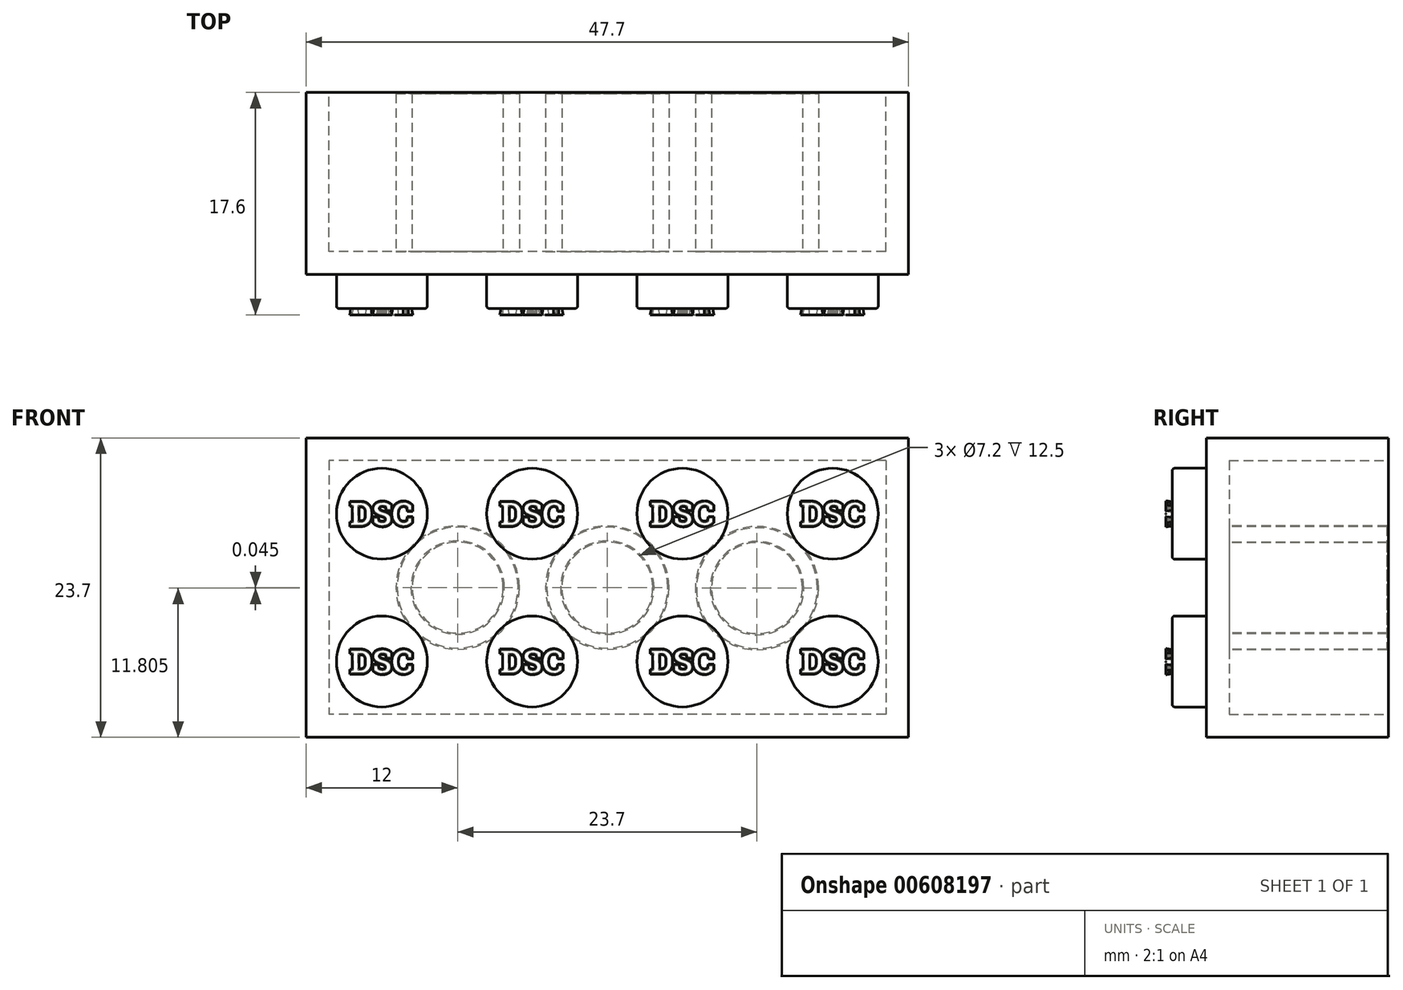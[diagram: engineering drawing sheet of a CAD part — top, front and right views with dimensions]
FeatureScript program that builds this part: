
annotation { "Feature Type Name" : "Feature", "Feature Type Description" : "" }
export const myFeature = defineFeature(function(context is Context, id is Id, definition is map)
    precondition{}
    {
        {
            var Q0;
            Q0=qCreatedBy(makeId("Front.planeOp"),FACE);
            var sketch = newSketch(context, id + "F0", { "sketchPlane" : qUnion([Q0])});
            skLineSegment(sketch, "E0.bottom", {"start": v(-23.85, 11.85) * mm, "end": v(23.85, 11.85) * mm});
            skLineSegment(sketch, "E0.top", {"start": v(-23.85, -11.85) * mm, "end": v(23.85, -11.85) * mm});
            skLineSegment(sketch, "E0.left", {"start": v(-23.85, 11.85) * mm, "end": v(-23.85, -11.85) * mm});
            skLineSegment(sketch, "E0.right", {"start": v(23.85, 11.85) * mm, "end": v(23.85, -11.85) * mm});
            skSolve(sketch);
        }
        {
            var Q0;
            Q0=makeQuery(id+"F0.imprint","IMPRINT",FACE,{"disambiguationData":[TD([[makeQuery(id+"F0.imprint","IMPRINT",EDGE,{"derivedFrom":sQuery(id+"F0.wireOp",EDGE,"E0.bottom")}),-1.0]])]});
            extrude(context, id + "F1", {"entities" : qUnion([Q0]), "depth" : 14.4 * mm, "offsetDistance" : 25 * mm});
        }
        {
            var Q0;
            Q0=makeQuery(id+"F1.opExtrude","CAP_FACE",FACE,{"disambiguationData":[OSD([sQuery(id+"F0.wireOp",EDGE,"E0.bottom"),sQuery(id+"F0.wireOp",EDGE,"E0.top"),sQuery(id+"F0.wireOp",EDGE,"E0.left"),sQuery(id+"F0.wireOp",EDGE,"E0.right")])],"isStart":true});
            var sketch = newSketch(context, id + "F2", { "sketchPlane" : qUnion([Q0])});
            skLineSegment(sketch, "E1.bottom", {"start": v(-22.05, 10.05) * mm, "end": v(22.05, 10.05) * mm});
            skLineSegment(sketch, "E1.top", {"start": v(-22.05, -10.05) * mm, "end": v(22.05, -10.05) * mm});
            skLineSegment(sketch, "E1.left", {"start": v(-22.05, 10.05) * mm, "end": v(-22.05, -10.05) * mm});
            skLineSegment(sketch, "E1.right", {"start": v(22.05, 10.05) * mm, "end": v(22.05, -10.05) * mm});
            skSolve(sketch);
        }
        {
            var Q0;
            Q0=makeQuery(id+"F2.imprint","IMPRINT",FACE,{"disambiguationData":[TD([[makeQuery(id+"F2.imprint","IMPRINT",EDGE,{"derivedFrom":sQuery(id+"F2.wireOp",EDGE,"E1.bottom")}),-1.0]])]});
            extrude(context, id + "F3", {"entities" : qUnion([Q0]), "operationType" : NewBodyOperationType.REMOVE, "oppositeDirection" : true, "depth" : 12.6 * mm, "offsetDistance" : 25 * mm});
        }
        {
            var Q0;
            Q0=makeQuery(id+"F1.opExtrude","CAP_FACE",FACE,{"disambiguationData":[OSD([sQuery(id+"F0.wireOp",EDGE,"E0.bottom"),sQuery(id+"F0.wireOp",EDGE,"E0.top"),sQuery(id+"F0.wireOp",EDGE,"E0.left"),sQuery(id+"F0.wireOp",EDGE,"E0.right")])],"isStart":false});
            var sketch = newSketch(context, id + "F4", { "sketchPlane" : qUnion([Q0])});
            skCircle(sketch, "E2", {"center": v(-17.85, 5.85) * mm, "radius": 3.6 * mm});
            skCircle(sketch, "E3.1.0.0", {"center": v(-5.95, 5.85) * mm, "radius": 3.6 * mm});
            skCircle(sketch, "E3.2.0.0", {"center": v(5.95, 5.85) * mm, "radius": 3.6 * mm});
            skCircle(sketch, "E3.3.0.0", {"center": v(17.85, 5.85) * mm, "radius": 3.6 * mm});
            skLineSegment(sketch, "E3.direction1", {"start": v(-17.85, 5.85) * mm, "end": v(-5.95, 5.85) * mm, "construction": true});
            skCircle(sketch, "E4", {"center": v(-17.85, -5.85) * mm, "radius": 3.6 * mm});
            skCircle(sketch, "E5.1.0.0", {"center": v(-5.95, -5.85) * mm, "radius": 3.6 * mm});
            skCircle(sketch, "E5.2.0.0", {"center": v(5.95, -5.85) * mm, "radius": 3.6 * mm});
            skLineSegment(sketch, "E5.direction1", {"start": v(-17.85, -5.85) * mm, "end": v(-5.95, -5.85) * mm, "construction": true});
            skCircle(sketch, "E6.0.3.0", {"center": v(17.85, -5.85) * mm, "radius": 3.6 * mm});
            skSolve(sketch);
        }
        {
            var Q0;
            Q0=makeQuery(id+"F4.imprint","IMPRINT",FACE,{"disambiguationData":[TD([[makeQuery(id+"F4.imprint","IMPRINT",EDGE,{"derivedFrom":sQuery(id+"F4.wireOp",EDGE,"E2")}),1.0]])]});
            var Q1;
            Q1=makeQuery(id+"F4.imprint","IMPRINT",FACE,{"disambiguationData":[TD([[makeQuery(id+"F4.imprint","IMPRINT",EDGE,{"derivedFrom":sQuery(id+"F4.wireOp",EDGE,"E3.1.0.0")}),1.0]])]});
            var Q2;
            Q2=makeQuery(id+"F4.imprint","IMPRINT",FACE,{"disambiguationData":[TD([[makeQuery(id+"F4.imprint","IMPRINT",EDGE,{"derivedFrom":sQuery(id+"F4.wireOp",EDGE,"E3.2.0.0")}),1.0]])]});
            var Q3;
            Q3=makeQuery(id+"F4.imprint","IMPRINT",FACE,{"disambiguationData":[TD([[makeQuery(id+"F4.imprint","IMPRINT",EDGE,{"derivedFrom":sQuery(id+"F4.wireOp",EDGE,"E3.3.0.0")}),1.0]])]});
            var Q4;
            Q4=makeQuery(id+"F4.imprint","IMPRINT",FACE,{"disambiguationData":[TD([[makeQuery(id+"F4.imprint","IMPRINT",EDGE,{"derivedFrom":sQuery(id+"F4.wireOp",EDGE,"E4")}),1.0]])]});
            var Q5;
            Q5=makeQuery(id+"F4.imprint","IMPRINT",FACE,{"disambiguationData":[TD([[makeQuery(id+"F4.imprint","IMPRINT",EDGE,{"derivedFrom":sQuery(id+"F4.wireOp",EDGE,"E5.1.0.0")}),1.0]])]});
            var Q6;
            Q6=makeQuery(id+"F4.imprint","IMPRINT",FACE,{"disambiguationData":[TD([[makeQuery(id+"F4.imprint","IMPRINT",EDGE,{"derivedFrom":sQuery(id+"F4.wireOp",EDGE,"E5.2.0.0")}),1.0]])]});
            var Q7;
            Q7=makeQuery(id+"F4.imprint","IMPRINT",FACE,{"disambiguationData":[TD([[makeQuery(id+"F4.imprint","IMPRINT",EDGE,{"derivedFrom":sQuery(id+"F4.wireOp",EDGE,"E6.0.3.0")}),1.0]])]});
            extrude(context, id + "F5", {"entities" : qUnion([Q0, Q1, Q2, Q3, Q4, Q5, Q6, Q7]), "depth" : 2.7 * mm, "offsetDistance" : 25 * mm});
        }
        {
            var Q0;
            Q0=makeQuery(id+"F5.opExtrude","CAP_FACE",FACE,{"disambiguationData":[OSD([sQuery(id+"F4.wireOp",EDGE,"E2")])],"isStart":false});
            var sketch = newSketch(context, id + "F6", { "sketchPlane" : qUnion([Q0])});
            skText(sketch, "E7", { "text": "DSC", "fontName": "RobotoSlab-Bold.ttf"});
            skPoint(sketch, "E8", {"position": v(-17.85, 5.85) * mm});
            skText(sketch, "E9", { "text": "DSC", "fontName": "RobotoSlab-Bold.ttf"});
            skPoint(sketch, "E10", {"position": v(-17.85, -5.85) * mm});
            skText(sketch, "E11", { "text": "DSC", "fontName": "RobotoSlab-Bold.ttf"});
            skPoint(sketch, "E12", {"position": v(-5.95, -5.85) * mm});
            skText(sketch, "E13", { "text": "DSC", "fontName": "RobotoSlab-Bold.ttf"});
            skPoint(sketch, "E14", {"position": v(-5.95, 5.85) * mm});
            skText(sketch, "E15", { "text": "DSC", "fontName": "RobotoSlab-Bold.ttf"});
            skPoint(sketch, "E16", {"position": v(5.95, 5.85) * mm});
            skPoint(sketch, "E17", {"position": v(5.95, -5.85) * mm});
            skPoint(sketch, "E18", {"position": v(17.85, 5.82) * mm});
            skText(sketch, "E19", { "text": "DSC", "fontName": "RobotoSlab-Bold.ttf"});
            skPoint(sketch, "E20", {"position": v(17.85, -5.85) * mm});
            skText(sketch, "E21", { "text": "DSC", "fontName": "RobotoSlab-Bold.ttf"});
            skPoint(sketch, "E22", {"position": v(17.85, 5.85) * mm});
            skText(sketch, "E23", { "text": "DSC", "fontName": "RobotoSlab-Bold.ttf"});
            const initialGuessF6  = {"E7": [-0.02038, 0.00492, 1, 0, 0.00185], "E9": [-0.02038, -0.00678, 1, 0, 0.00185], "E11": [-0.00848, -0.00678, 1, 0, 0.00185], "E13": [-0.00848, 0.00492, 1, 0, 0.00185], "E15": [0.00342, 0.00492, 1, 0, 0.00186], "E19": [0.01532, -0.00678, 1, 0, 0.00186], "E21": [0.01532, 0.00492, 1, 0, 0.00186], "E23": [0.00342, -0.00678, 1, 0, 0.00186]};
            skSetInitialGuess(sketch, initialGuessF6);
            skSolve(sketch);
        }
        {
            var Q0;
            Q0 = qSketchRegion(id + "F6", true);
            extrude(context, id + "F7", {"entities" : qUnion([Q0]), "depth" : 0.5 * mm, "offsetDistance" : 25 * mm, "hasDraft" : true, "draftAngle" : 10 * degree});
        }
        {
            var Q0;
            Q0=makeQuery(id+"F5.opExtrude","CAP_EDGE",EDGE,{"disambiguationData":[OSD([sQuery(id+"F4.wireOp",EDGE,"E2")])],"isStart":false});
            var Q1;
            Q1=makeQuery(id+"F5.opExtrude","CAP_EDGE",EDGE,{"disambiguationData":[OSD([sQuery(id+"F4.wireOp",EDGE,"E3.1.0.0")])],"isStart":false});
            var Q2;
            Q2=makeQuery(id+"F5.opExtrude","CAP_EDGE",EDGE,{"disambiguationData":[OSD([sQuery(id+"F4.wireOp",EDGE,"E3.2.0.0")])],"isStart":false});
            var Q3;
            Q3=makeQuery(id+"F5.opExtrude","CAP_EDGE",EDGE,{"disambiguationData":[OSD([sQuery(id+"F4.wireOp",EDGE,"E3.3.0.0")])],"isStart":false});
            var Q4;
            Q4=makeQuery(id+"F5.opExtrude","CAP_EDGE",EDGE,{"disambiguationData":[OSD([sQuery(id+"F4.wireOp",EDGE,"E6.0.3.0")])],"isStart":false});
            var Q5;
            Q5=makeQuery(id+"F5.opExtrude","CAP_EDGE",EDGE,{"disambiguationData":[OSD([sQuery(id+"F4.wireOp",EDGE,"E5.2.0.0")])],"isStart":false});
            var Q6;
            Q6=makeQuery(id+"F5.opExtrude","CAP_EDGE",EDGE,{"disambiguationData":[OSD([sQuery(id+"F4.wireOp",EDGE,"E5.1.0.0")])],"isStart":false});
            var Q7;
            Q7=makeQuery(id+"F5.opExtrude","CAP_EDGE",EDGE,{"disambiguationData":[OSD([sQuery(id+"F4.wireOp",EDGE,"E4")])],"isStart":false});
            fillet(context, id + "F8", {"entities" : qUnion([Q0, Q1, Q2, Q3, Q4, Q5, Q6, Q7]), "radius" : 0.2 * mm, "tangentPropagation" : true, "allowEdgeOverflow" : false});
        }
        {
            var Q0;
            Q0=makeQuery(id+"F3.boolean.opBoolean","COPY",FACE,{"derivedFrom":makeQuery(id+"F3.opExtrude","CAP_FACE",FACE,{"disambiguationData":[OSD([sQuery(id+"F2.wireOp",EDGE,"E1.bottom"),sQuery(id+"F2.wireOp",EDGE,"E1.top"),sQuery(id+"F2.wireOp",EDGE,"E1.left"),sQuery(id+"F2.wireOp",EDGE,"E1.right")])],"isStart":false})});
            var sketch = newSketch(context, id + "F9", { "sketchPlane" : qUnion([Q0])});
            skCircle(sketch, "E24", {"center": v(11.85, 0) * mm, "radius": 4.88 * mm});
            skCircle(sketch, "E25", {"center": v(-11.85, -0.04) * mm, "radius": 4.88 * mm});
            skCircle(sketch, "E26", {"center": v(0, 0) * mm, "radius": 4.88 * mm});
            skSolve(sketch);
        }
        {
            var Q0;
            Q0=makeQuery(id+"F9.imprint","IMPRINT",FACE,{"disambiguationData":[TD([[makeQuery(id+"F9.imprint","IMPRINT",EDGE,{"derivedFrom":sQuery(id+"F9.wireOp",EDGE,"E25")}),1.0]])]});
            var Q1;
            Q1=makeQuery(id+"F9.imprint","IMPRINT",FACE,{"disambiguationData":[TD([[makeQuery(id+"F9.imprint","IMPRINT",EDGE,{"derivedFrom":sQuery(id+"F9.wireOp",EDGE,"E26")}),1.0]])]});
            var Q2;
            Q2=makeQuery(id+"F9.imprint","IMPRINT",FACE,{"disambiguationData":[TD([[makeQuery(id+"F9.imprint","IMPRINT",EDGE,{"derivedFrom":sQuery(id+"F9.wireOp",EDGE,"E24")}),1.0]])]});
            extrude(context, id + "F10", {"entities" : qUnion([Q0, Q1, Q2]), "operationType" : NewBodyOperationType.ADD, "depth" : 12.6 * mm, "offsetDistance" : 25 * mm});
        }
        {
            var Q0;
            Q0=makeQuery(id+"F3.boolean.opBoolean","COPY",FACE,{"derivedFrom":makeQuery(id+"F3.opExtrude","CAP_FACE",FACE,{"disambiguationData":[OSD([sQuery(id+"F2.wireOp",EDGE,"E1.bottom"),sQuery(id+"F2.wireOp",EDGE,"E1.top"),sQuery(id+"F2.wireOp",EDGE,"E1.left"),sQuery(id+"F2.wireOp",EDGE,"E1.right")])],"isStart":false})});
            var sketch = newSketch(context, id + "F11", { "sketchPlane" : qUnion([Q0])});
            skPoint(sketch, "E27", {"position": v(-11.85, -0.04) * mm});
            skPoint(sketch, "E28", {"position": v(11.85, 0) * mm});
            skCircle(sketch, "E29", {"center": v(-11.85, -0.04) * mm, "radius": 3.6 * mm});
            skCircle(sketch, "E30", {"center": v(0, 0) * mm, "radius": 3.6 * mm});
            skCircle(sketch, "E31", {"center": v(11.85, 0) * mm, "radius": 3.6 * mm});
            skSolve(sketch);
        }
        {
            var Q0;
            Q0 = qSketchRegion(id + "F11", true);
            extrude(context, id + "F12", {"entities" : qUnion([Q0]), "operationType" : NewBodyOperationType.REMOVE, "oppositeDirection" : true, "depth" : -15 * mm, "offsetDistance" : 25 * mm});
        }
        {
            var Q0;
            Q0=makeQuery(id+"F10.opExtrude","CAP_EDGE",EDGE,{"disambiguationData":[OSD([sQuery(id+"F9.wireOp",EDGE,"E25")])],"isStart":false});
            var Q1;
            Q1=makeQuery(id+"F12.boolean.opBoolean","INTERSECT",EDGE,{"derivedFrom":[makeQuery(id+"F10.opExtrude","CAP_FACE",FACE,{"disambiguationData":[OSD([sQuery(id+"F9.wireOp",EDGE,"E25")])],"isStart":false}),makeQuery(id+"F12.opExtrude","SWEPT_FACE",FACE,{"disambiguationData":[OSD([sQuery(id+"F11.wireOp",EDGE,"E29")])]})]});
            var Q2;
            Q2=makeQuery(id+"F10.opExtrude","CAP_EDGE",EDGE,{"disambiguationData":[OSD([sQuery(id+"F9.wireOp",EDGE,"E26")])],"isStart":false});
            var Q3;
            Q3=makeQuery(id+"F12.boolean.opBoolean","INTERSECT",EDGE,{"derivedFrom":[makeQuery(id+"F10.opExtrude","CAP_FACE",FACE,{"disambiguationData":[OSD([sQuery(id+"F9.wireOp",EDGE,"E26")])],"isStart":false}),makeQuery(id+"F12.opExtrude","SWEPT_FACE",FACE,{"disambiguationData":[OSD([sQuery(id+"F11.wireOp",EDGE,"E30")])]})]});
            var Q4;
            Q4=makeQuery(id+"F10.opExtrude","CAP_EDGE",EDGE,{"disambiguationData":[OSD([sQuery(id+"F9.wireOp",EDGE,"E24")])],"isStart":false});
            var Q5;
            Q5=makeQuery(id+"F12.boolean.opBoolean","INTERSECT",EDGE,{"derivedFrom":[makeQuery(id+"F10.opExtrude","CAP_FACE",FACE,{"disambiguationData":[OSD([sQuery(id+"F9.wireOp",EDGE,"E24")])],"isStart":false}),makeQuery(id+"F12.opExtrude","SWEPT_FACE",FACE,{"disambiguationData":[OSD([sQuery(id+"F11.wireOp",EDGE,"E31")])]})]});
            var Q6;
            Q6=makeQuery(id+"F3.boolean.opBoolean","COPY",EDGE,{"derivedFrom":makeQuery(id+"F3.opExtrude","CAP_EDGE",EDGE,{"disambiguationData":[OSD([sQuery(id+"F2.wireOp",EDGE,"E1.bottom")])],"isStart":true})});
            var Q7;
            Q7=makeQuery(id+"F3.boolean.opBoolean","COPY",EDGE,{"derivedFrom":makeQuery(id+"F3.opExtrude","CAP_EDGE",EDGE,{"disambiguationData":[OSD([sQuery(id+"F2.wireOp",EDGE,"E1.right")])],"isStart":true})});
            var Q8;
            Q8=makeQuery(id+"F3.boolean.opBoolean","COPY",EDGE,{"derivedFrom":makeQuery(id+"F3.opExtrude","CAP_EDGE",EDGE,{"disambiguationData":[OSD([sQuery(id+"F2.wireOp",EDGE,"E1.top")])],"isStart":true})});
            var Q9;
            Q9=makeQuery(id+"F3.boolean.opBoolean","COPY",EDGE,{"derivedFrom":makeQuery(id+"F3.opExtrude","CAP_EDGE",EDGE,{"disambiguationData":[OSD([sQuery(id+"F2.wireOp",EDGE,"E1.left")])],"isStart":true})});
            chamfer(context, id + "F13", {"entities" : qUnion([Q0, Q1, Q2, Q3, Q4, Q5, Q6, Q7, Q8, Q9]), "width" : 0.1 * mm, "tangentPropagation" : true});
        }
    });
